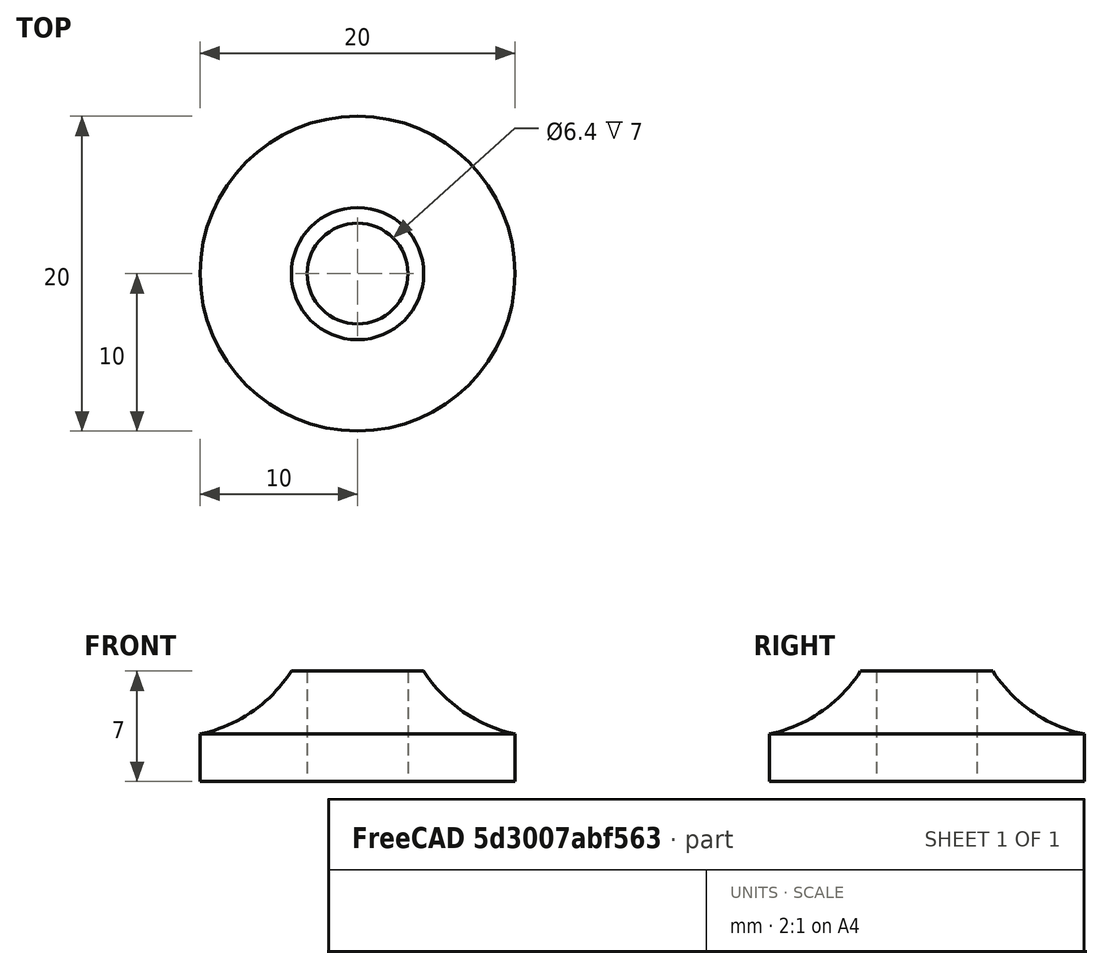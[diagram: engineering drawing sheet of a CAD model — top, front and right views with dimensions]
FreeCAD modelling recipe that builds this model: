
FCSTD DOCUMENT  (FreeCAD 1.1R38991 (Git))
Label: PG01 - Varier Thatsit Balans - knee level locking washer.20241019
License: All rights reserved
LicenseURL: https://en.wikipedia.org/wiki/All_rights_reserved
objects: Sketcher::SketchObject×1, PartDesign::Revolution×1, PartDesign::Body×1
note: 6 computed .brp shape members not serialized (recipe doc carries the construction recipe); baked Part::Feature solids carry a one-line shape summary decoded from their .brp

FEATURE [Sketcher::SketchObject] Sketch
  ArcFitTolerance = 1e-06
  AttachmentSupport = -> [XZ_Plane]
  FullyConstrained = true
  MakeInternals = false
  MapMode = 5
  Placement = pos=(0,0,0) rot=(1,0,0;1.5708rad)
  sketch-geometry (5):
    g0: LineSegment StartX=3.2 StartY=0 StartZ=0 EndX=10 EndY=0 EndZ=0
    g1: LineSegment StartX=10 StartY=0 StartZ=0 EndX=10 EndY=3 EndZ=0
    g2: LineSegment StartX=4.2 StartY=7 StartZ=0 EndX=3.2 EndY=7 EndZ=0
    g3: LineSegment StartX=3.2 StartY=7 StartZ=0 EndX=3.2 EndY=0 EndZ=0
    g4: ArcOfCircle CenterX=11.9276 CenterY=12 CenterZ=0 NormalX=0 NormalY=0 NormalZ=1 AngleXU=0 Radius=9.20411 StartAngle=3.71588 EndAngle=4.5014
  constraints (16):
    c: PointOnObject(g0,g-1)
    c: Horizontal(g0)
    c: Coincident(g0,g1)
    c: Vertical(g1)
    c: Horizontal(g2)
    c: Coincident(g2,g3)
    c: Coincident(g3,g0)
    c: Vertical(g3)
    c: DistanceX(g-1,g0) = 3.2
    c: DistanceY(g0,g2) = 7
    c: DistanceY(g0,g1) = 3
    c: Distance(g0,g-2) = 10
    c: Distance(g2,g2) = 1
    c: Coincident(g4,g2)
    c: Coincident(g4,g1)
    c: DistanceY(g-1,g4) = 12
FEATURE [PartDesign::Revolution] Revolution
  Angle = 360
  Angle2 = 60
  Axis = (1e-16,1e-16,1)
  Base = (0,0,0)
  Placement = pos=(0,0,0) rot=(1,0,0;1.5708rad)
  Profile = -> Sketch
  ReferenceAxis = -> Z_Axis
  Refine = true
  Reversed = true
  Suppressed = false
  Type = 0
FEATURE [PartDesign::Body] Body
  AllowCompound = true
  Group = -> [Sketch,Revolution]
  Origin = -> Origin
  Tip = -> Revolution
